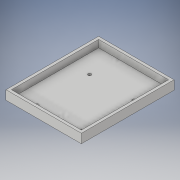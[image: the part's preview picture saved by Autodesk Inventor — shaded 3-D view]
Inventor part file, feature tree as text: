
AUTODESK INVENTOR PART (.ipt)
format: ipt  version: 2019.4 (Build 234330000, 330)  size: 122,880 bytes
history: native  units: mm
features: extrude x3, sketch x3
ambient origin geometry x8: Origin, YZ Plane, XZ Plane, XY Plane, X Axis, Y Axis, Z Axis, Center Point
bodies: Solid1 (feature_tree)
feature tree (6):
  extrude  "Extrusion1"  Depth=96.0mm
  extrude  "Extrusion2"  Depth=10.0mm TaperAngle=0.0deg
  extrude  "Extrusion3"  Depth=96.0mm
  sketch  "Sketch1"  dims[d0=77.0mm d1=96.0mm]
  sketch  "Sketch2"  dims[d2=3.0mm d3=10.0mm d4=0.0mm]
  sketch  "Sketch3"  dims[d5=77.0mm d6=96.0mm d7=8.0mm d8=0.0mm d9=7.5mm d10=7.5mm d11=3.5mm d12=20.0mm d14=58.0mm d15=20.0mm d17=49.0mm d20=3.0mm d21=0.0mm]
